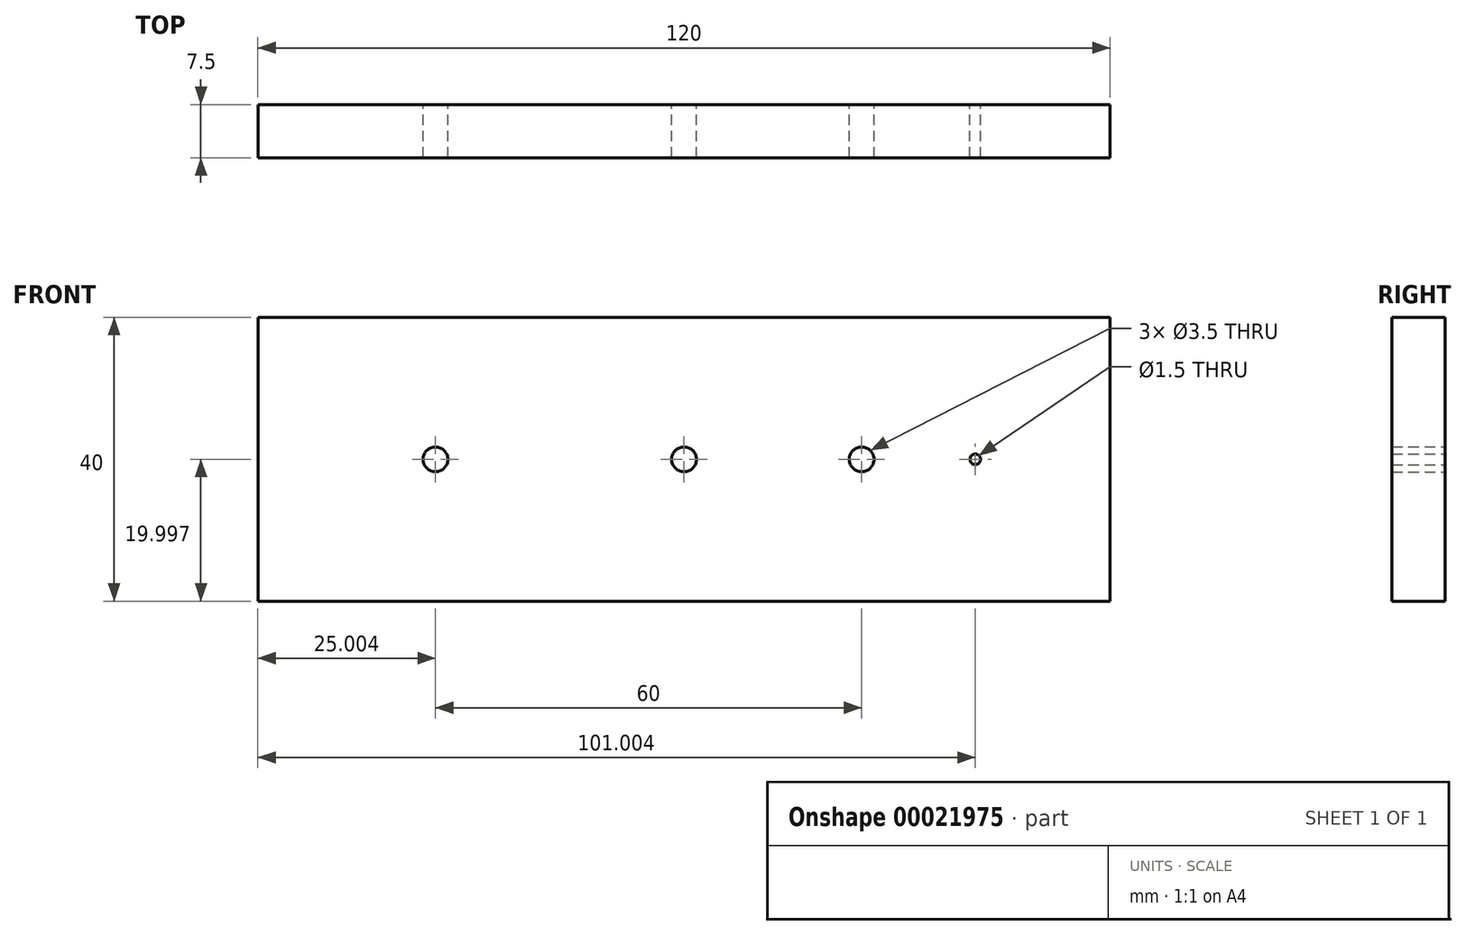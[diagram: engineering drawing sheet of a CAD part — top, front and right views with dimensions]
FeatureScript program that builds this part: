
annotation { "Feature Type Name" : "Feature", "Feature Type Description" : "" }
export const myFeature = defineFeature(function(context is Context, id is Id, definition is map)
    precondition{}
    {
        {
            var Q0;
            Q0=qCreatedBy(makeId("Front.planeOp"),FACE);
            var sketch = newSketch(context, id + "F0", { "sketchPlane" : qUnion([Q0])});
            skLineSegment(sketch, "E0.bottom", {"start": v(-48.62, 19.73) * mm, "end": v(71.38, 19.73) * mm});
            skLineSegment(sketch, "E0.top", {"start": v(-48.62, -20.27) * mm, "end": v(71.38, -20.27) * mm});
            skLineSegment(sketch, "E0.left", {"start": v(-48.62, 19.73) * mm, "end": v(-48.62, -20.27) * mm});
            skLineSegment(sketch, "E0.right", {"start": v(71.38, 19.73) * mm, "end": v(71.38, -20.27) * mm});
            skLineSegment(sketch, "E1", {"start": v(-48.62, -20.27) * mm, "end": v(-48.62, -0.27) * mm});
            skLineSegment(sketch, "E2", {"start": v(71.38, -20.27) * mm, "end": v(71.38, -0.27) * mm});
            skLineSegment(sketch, "E3", {"start": v(-48.62, -0.27) * mm, "end": v(71.38, -0.27) * mm});
            skLineSegment(sketch, "E4", {"start": v(-48.62, -0.27) * mm, "end": v(-23.62, -0.27) * mm});
            skCircle(sketch, "E5", {"center": v(-23.62, -0.27) * mm, "radius": 1.75 * mm});
            skLineSegment(sketch, "E6", {"start": v(-23.62, -0.27) * mm, "end": v(11.38, -0.27) * mm});
            skCircle(sketch, "E7", {"center": v(11.38, -0.27) * mm, "radius": 1.75 * mm});
            skLineSegment(sketch, "E8", {"start": v(11.38, -0.27) * mm, "end": v(36.38, -0.27) * mm});
            skLineSegment(sketch, "E9", {"start": v(36.38, -0.27) * mm, "end": v(52.38, -0.27) * mm});
            skCircle(sketch, "E10", {"center": v(36.38, -0.27) * mm, "radius": 1.75 * mm});
            skCircle(sketch, "E11", {"center": v(52.38, -0.27) * mm, "radius": 0.75 * mm});
            skSolve(sketch);
        }
        {
            var Q0;
            Q0 = qSketchRegion(id + "F0", true);
            extrude(context, id + "F1", {"entities" : qUnion([Q0]), "depth" : 7.5 * mm});
        }
    });
